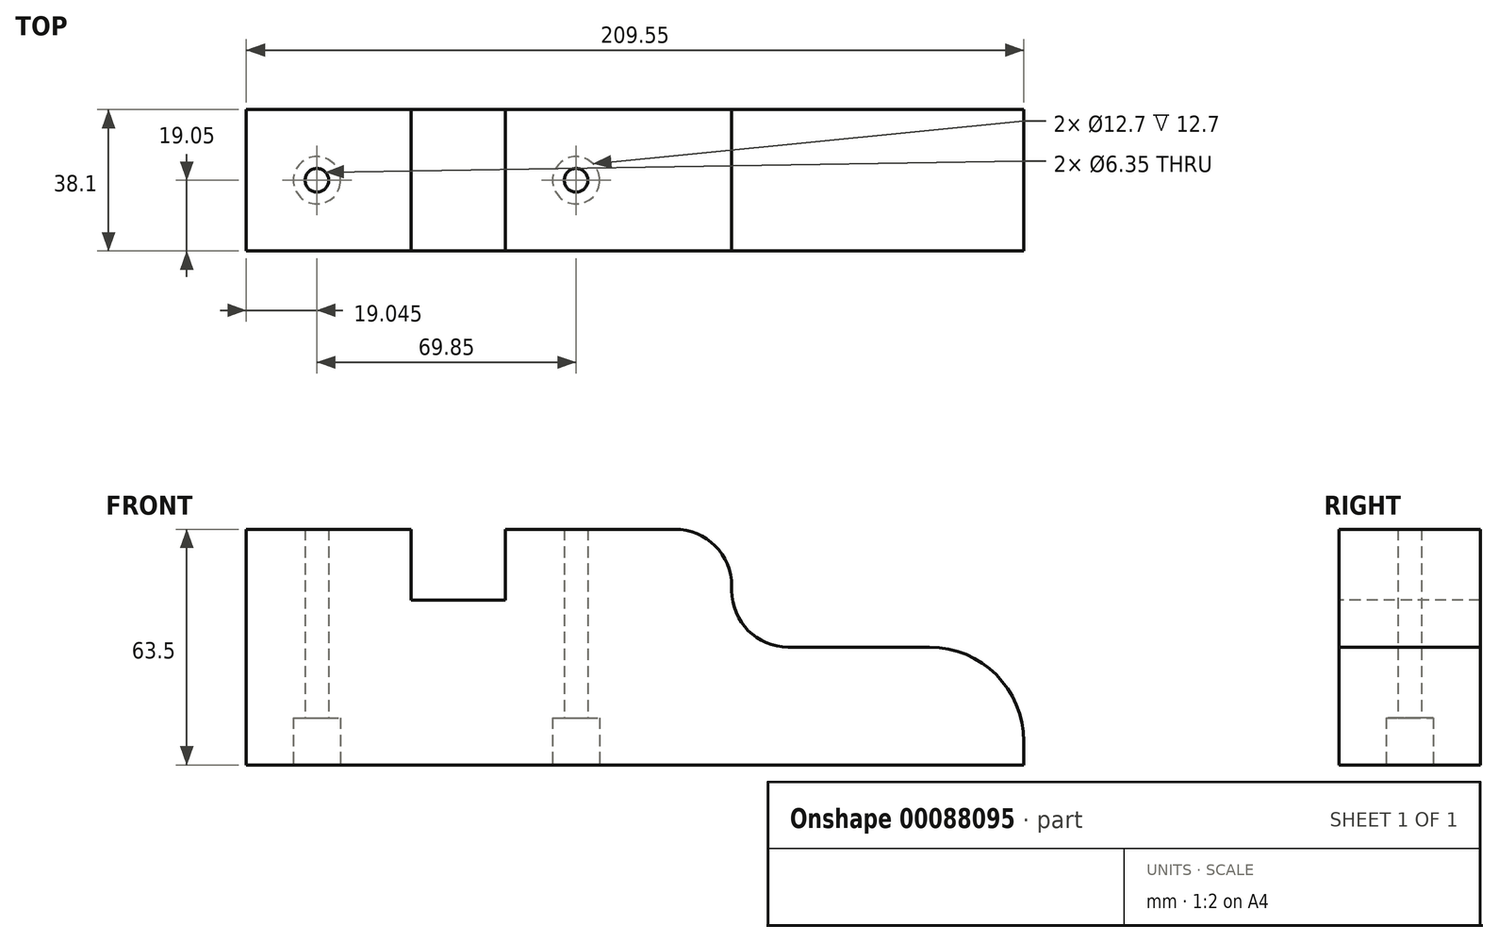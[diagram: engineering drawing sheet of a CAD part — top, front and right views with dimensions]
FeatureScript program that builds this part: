
annotation { "Feature Type Name" : "Feature", "Feature Type Description" : "" }
export const myFeature = defineFeature(function(context is Context, id is Id, definition is map)
    precondition{}
    {
        {
            var Q0;
            Q0=qCreatedBy(makeId("Right.planeOp"),FACE);
            var sketch = newSketch(context, id + "F0", { "sketchPlane" : qUnion([Q0])});
            skLineSegment(sketch, "E0.bottom", {"start": v(-19.05, 31.75) * mm, "end": v(19.05, 31.75) * mm});
            skLineSegment(sketch, "E0.top", {"start": v(-19.05, -31.75) * mm, "end": v(19.05, -31.75) * mm});
            skLineSegment(sketch, "E0.left", {"start": v(-19.05, 31.75) * mm, "end": v(-19.05, -31.75) * mm});
            skLineSegment(sketch, "E0.right", {"start": v(19.05, 31.75) * mm, "end": v(19.05, -31.75) * mm});
            skSolve(sketch);
        }
        {
            var Q0;
            Q0=makeQuery(id+"F0.imprint","IMPRINT",FACE,{"disambiguationData":[TD([[makeQuery(id+"F0.imprint","IMPRINT",EDGE,{"derivedFrom":sQuery(id+"F0.wireOp",EDGE,"E0.bottom")}),-1.0]])]});
            extrude(context, id + "F1", {"entities" : qUnion([Q0]), "endBound" : BoundingType.SYMMETRIC, "depth" : 209.55 * mm});
        }
        {
            var Q0;
            Q0=makeQuery(id+"F1.opExtrude","SWEPT_FACE",FACE,{"disambiguationData":[OSD([sQuery(id+"F0.wireOp",EDGE,"E0.left")])]});
            var sketch = newSketch(context, id + "F2", { "sketchPlane" : qUnion([Q0])});
            skLineSegment(sketch, "E1", {"start": v(114.5, -25.4) * mm, "end": v(104.78, -25.4) * mm, "construction": true});
            skLineSegment(sketch, "E2", {"start": v(114.5, 15.24) * mm, "end": v(104.78, 15.24) * mm, "construction": true});
            skLineSegment(sketch, "E3", {"start": v(114.07, 16.5) * mm, "end": v(104.78, 16.5) * mm, "construction": true});
            skLineSegment(sketch, "E4", {"start": v(104.78, 0) * mm, "end": v(86.03, 0) * mm, "construction": true});
            skLineSegment(sketch, "E5", {"start": v(79.38, 0) * mm, "end": v(79.38, -31.75) * mm, "construction": true});
            skLineSegment(sketch, "E6", {"start": v(41.28, 31.75) * mm, "end": v(41.28, -31.75) * mm, "construction": true});
            skLineSegment(sketch, "E7", {"start": v(26.04, 31.75) * mm, "end": v(26.04, -31.75) * mm, "construction": true});
            skLineSegment(sketch, "E8", {"start": v(10.8, 31.75) * mm, "end": v(10.8, -31.75) * mm, "construction": true});
            skArc(sketch, "E9", {"start": v(104.78, -25.4) * mm, "mid": v(97.34, -7.44) * mm, "end": v(79.38, 0) * mm});
            skArc(sketch, "E10", {"start": v(41.28, 0) * mm, "mid": v(30.5, 4.46) * mm, "end": v(26.04, 15.24) * mm});
            skArc(sketch, "E11", {"start": v(26.04, 16.5) * mm, "mid": v(21.57, 27.29) * mm, "end": v(10.8, 31.75) * mm});
            skLineSegment(sketch, "E12", {"start": v(26.04, 16.5) * mm, "end": v(26.04, 15.24) * mm});
            skLineSegment(sketch, "E13", {"start": v(41.28, 0) * mm, "end": v(79.38, 0) * mm});
            skLineSegment(sketch, "E14", {"start": v(10.8, 31.75) * mm, "end": v(104.78, 31.75) * mm});
            skLineSegment(sketch, "E15", {"start": v(104.78, 31.75) * mm, "end": v(104.78, -25.4) * mm});
            skSolve(sketch);
        }
        {
            var Q0;
            Q0=makeQuery(id+"F2.imprint","IMPRINT",FACE,{"disambiguationData":[TD([[makeQuery(id+"F2.imprint","IMPRINT",EDGE,{"derivedFrom":sQuery(id+"F2.wireOp",EDGE,"E9")}),-1.0]])]});
            extrude(context, id + "F3", {"entities" : qUnion([Q0]), "operationType" : NewBodyOperationType.REMOVE, "endBound" : BoundingType.THROUGH_ALL, "oppositeDirection" : true, "depth" : 25.4 * mm});
        }
        {
            var Q0;
            Q0=makeQuery(id+"F1.opExtrude","SWEPT_FACE",FACE,{"disambiguationData":[OSD([sQuery(id+"F0.wireOp",EDGE,"E0.top")])]});
            var sketch = newSketch(context, id + "F4", { "sketchPlane" : qUnion([Q0])});
            skLineSegment(sketch, "E16", {"start": v(-85.73, 19.05) * mm, "end": v(-85.73, -19.05) * mm, "construction": true});
            skLineSegment(sketch, "E17", {"start": v(-15.88, 19.05) * mm, "end": v(-15.87, -19.05) * mm, "construction": true});
            skLineSegment(sketch, "E18", {"start": v(1.34, 0) * mm, "end": v(104.78, 0) * mm, "construction": true});
            skLineSegment(sketch, "E19", {"start": v(3.17, 19.05) * mm, "end": v(3.17, -19.05) * mm, "construction": true});
            skCircle(sketch, "E20", {"center": v(-85.73, 0) * mm, "radius": 6.35 * mm});
            skCircle(sketch, "E21", {"center": v(-15.88, 0) * mm, "radius": 6.35 * mm});
            skSolve(sketch);
        }
        {
            var Q0;
            Q0=makeQuery(id+"F4.imprint","IMPRINT",FACE,{"disambiguationData":[TD([[makeQuery(id+"F4.imprint","IMPRINT",EDGE,{"derivedFrom":sQuery(id+"F4.wireOp",EDGE,"E20")}),1.0]])]});
            var Q1;
            Q1=makeQuery(id+"F4.imprint","IMPRINT",FACE,{"disambiguationData":[TD([[makeQuery(id+"F4.imprint","IMPRINT",EDGE,{"derivedFrom":sQuery(id+"F4.wireOp",EDGE,"E21")}),1.0]])]});
            extrude(context, id + "F5", {"entities" : qUnion([Q0, Q1]), "operationType" : NewBodyOperationType.REMOVE, "oppositeDirection" : true, "depth" : 12.7 * mm});
        }
        {
            var Q0;
            Q0=makeQuery(id+"F5.boolean.opBoolean","COPY",FACE,{"derivedFrom":makeQuery(id+"F5.opExtrude","CAP_FACE",FACE,{"disambiguationData":[OSD([sQuery(id+"F4.wireOp",EDGE,"E20")])],"isStart":false})});
            var sketch = newSketch(context, id + "F6", { "sketchPlane" : qUnion([Q0])});
            skCircle(sketch, "E22.0", {"center": v(-85.73, 0) * mm, "radius": 6.35 * mm});
            skCircle(sketch, "E23.0", {"center": v(-15.88, 0) * mm, "radius": 6.35 * mm});
            skCircle(sketch, "E24", {"center": v(-85.73, 0) * mm, "radius": 3.18 * mm});
            skCircle(sketch, "E25", {"center": v(-15.88, 0) * mm, "radius": 3.18 * mm});
            skSolve(sketch);
        }
        {
            var Q0;
            Q0=makeQuery(id+"F6.imprint","IMPRINT",FACE,{"disambiguationData":[TD([[makeQuery(id+"F6.imprint","IMPRINT",EDGE,{"derivedFrom":sQuery(id+"F6.wireOp",EDGE,"E24")}),1.0]])]});
            var Q1;
            Q1=makeQuery(id+"F6.imprint","IMPRINT",FACE,{"disambiguationData":[TD([[makeQuery(id+"F6.imprint","IMPRINT",EDGE,{"derivedFrom":sQuery(id+"F6.wireOp",EDGE,"E25")}),1.0]])]});
            extrude(context, id + "F7", {"entities" : qUnion([Q0, Q1]), "operationType" : NewBodyOperationType.REMOVE, "endBound" : BoundingType.THROUGH_ALL, "oppositeDirection" : true, "depth" : 25.4 * mm});
        }
        {
            var Q0;
            Q0=makeQuery(id+"F1.opExtrude","SWEPT_FACE",FACE,{"disambiguationData":[OSD([sQuery(id+"F0.wireOp",EDGE,"E0.left")])]});
            var sketch = newSketch(context, id + "F8", { "sketchPlane" : qUnion([Q0])});
            skLineSegment(sketch, "E26", {"start": v(3.17, 31.75) * mm, "end": v(3.17, -31.75) * mm, "construction": true});
            skLineSegment(sketch, "E27", {"start": v(-47.63, 31.75) * mm, "end": v(-47.63, -31.75) * mm, "construction": true});
            skLineSegment(sketch, "E28", {"start": v(-104.78, 12.7) * mm, "end": v(-2.63, 12.7) * mm, "construction": true});
            skLineSegment(sketch, "E29.bottom", {"start": v(-60.33, 12.7) * mm, "end": v(-34.93, 12.7) * mm});
            skLineSegment(sketch, "E29.top", {"start": v(-60.33, 31.75) * mm, "end": v(-34.93, 31.75) * mm});
            skLineSegment(sketch, "E29.left", {"start": v(-60.33, 12.7) * mm, "end": v(-60.33, 31.75) * mm});
            skLineSegment(sketch, "E29.right", {"start": v(-34.93, 12.7) * mm, "end": v(-34.93, 31.75) * mm});
            skSolve(sketch);
        }
        {
            var Q0;
            Q0=makeQuery(id+"F8.imprint","IMPRINT",FACE,{"disambiguationData":[TD([[makeQuery(id+"F8.imprint","IMPRINT",EDGE,{"derivedFrom":sQuery(id+"F8.wireOp",EDGE,"E29.bottom")}),1.0]])]});
            extrude(context, id + "F9", {"entities" : qUnion([Q0]), "operationType" : NewBodyOperationType.REMOVE, "endBound" : BoundingType.THROUGH_ALL, "oppositeDirection" : true, "depth" : 25.4 * mm});
        }
    });
